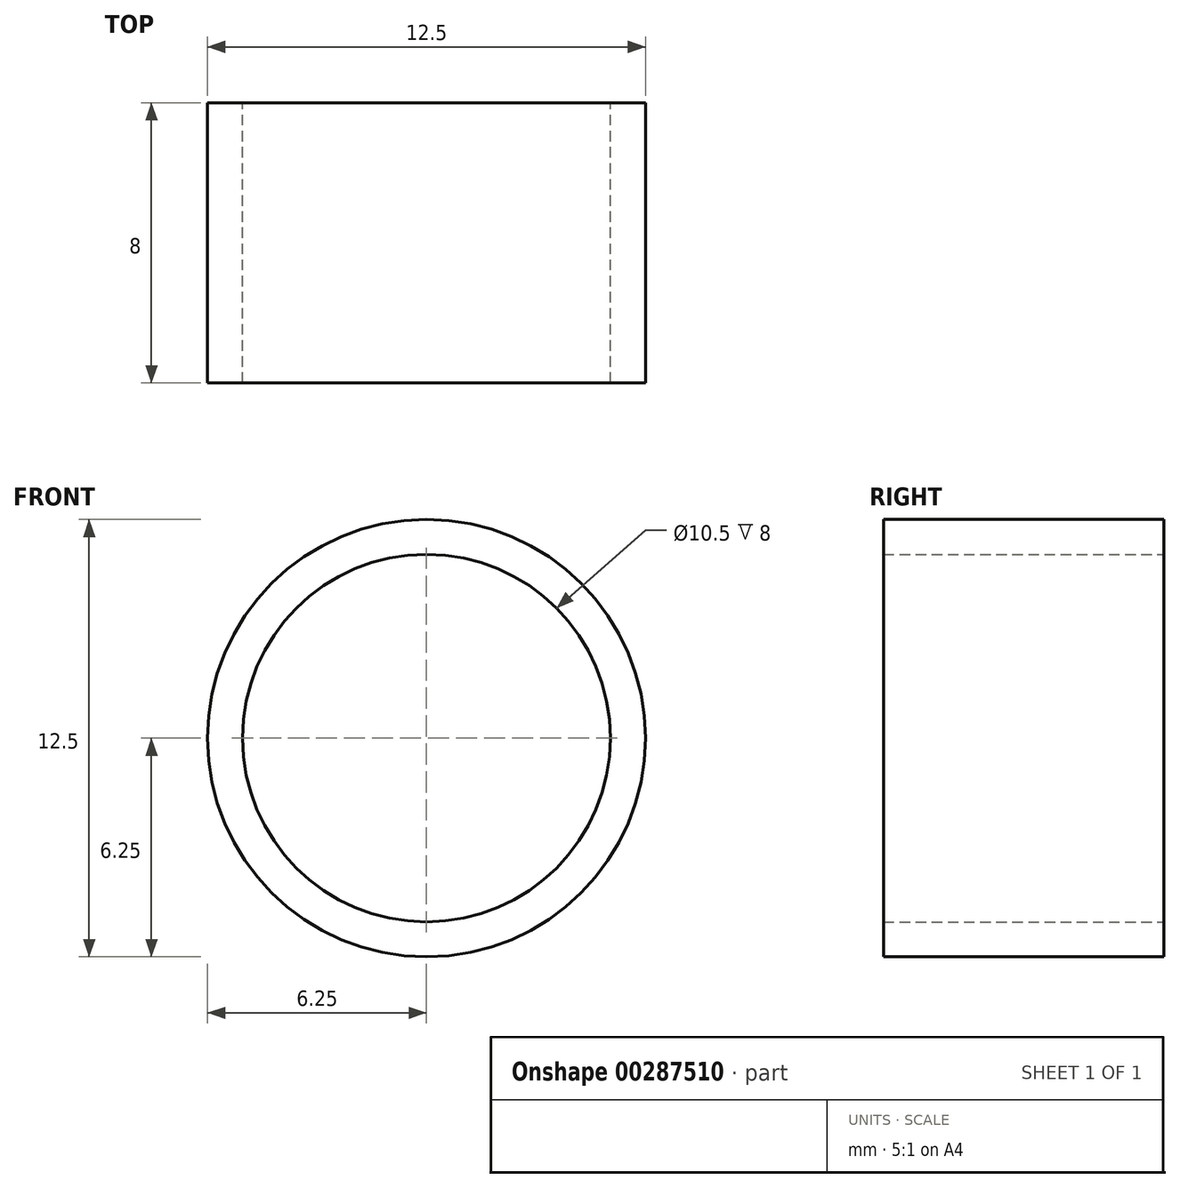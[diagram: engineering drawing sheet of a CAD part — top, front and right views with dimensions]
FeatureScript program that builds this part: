
annotation { "Feature Type Name" : "Feature", "Feature Type Description" : "" }
export const myFeature = defineFeature(function(context is Context, id is Id, definition is map)
    precondition{}
    {
        {
            var Q0;
            Q0=qCreatedBy(makeId("Front.planeOp"),FACE);
            var sketch = newSketch(context, id + "F0", { "sketchPlane" : qUnion([Q0])});
            skCircle(sketch, "E0", {"center": v(0, 0) * mm, "radius": 6.25 * mm});
            skSolve(sketch);
        }
        {
            var Q0;
            Q0=makeQuery(id+"F0.imprint","IMPRINT",FACE,{"disambiguationData":[TD([[makeQuery(id+"F0.imprint","IMPRINT",EDGE,{"derivedFrom":sQuery(id+"F0.wireOp",EDGE,"E0")}),1.0]])]});
            extrude(context, id + "F1", {"entities" : qUnion([Q0]), "depth" : 8 * mm});
        }
        {
            var Q0;
            Q0=makeQuery(id+"F1.opExtrude","CAP_FACE",FACE,{"disambiguationData":[OSD([sQuery(id+"F0.wireOp",EDGE,"E0")])],"isStart":true});
            var Q1;
            Q1=makeQuery(id+"F1.opExtrude","CAP_FACE",FACE,{"disambiguationData":[OSD([sQuery(id+"F0.wireOp",EDGE,"E0")])],"isStart":false});
            shell(context, id + "F2", {"entities" : qUnion([Q0, Q1]), "thickness" : 1 * mm});
        }
    });
